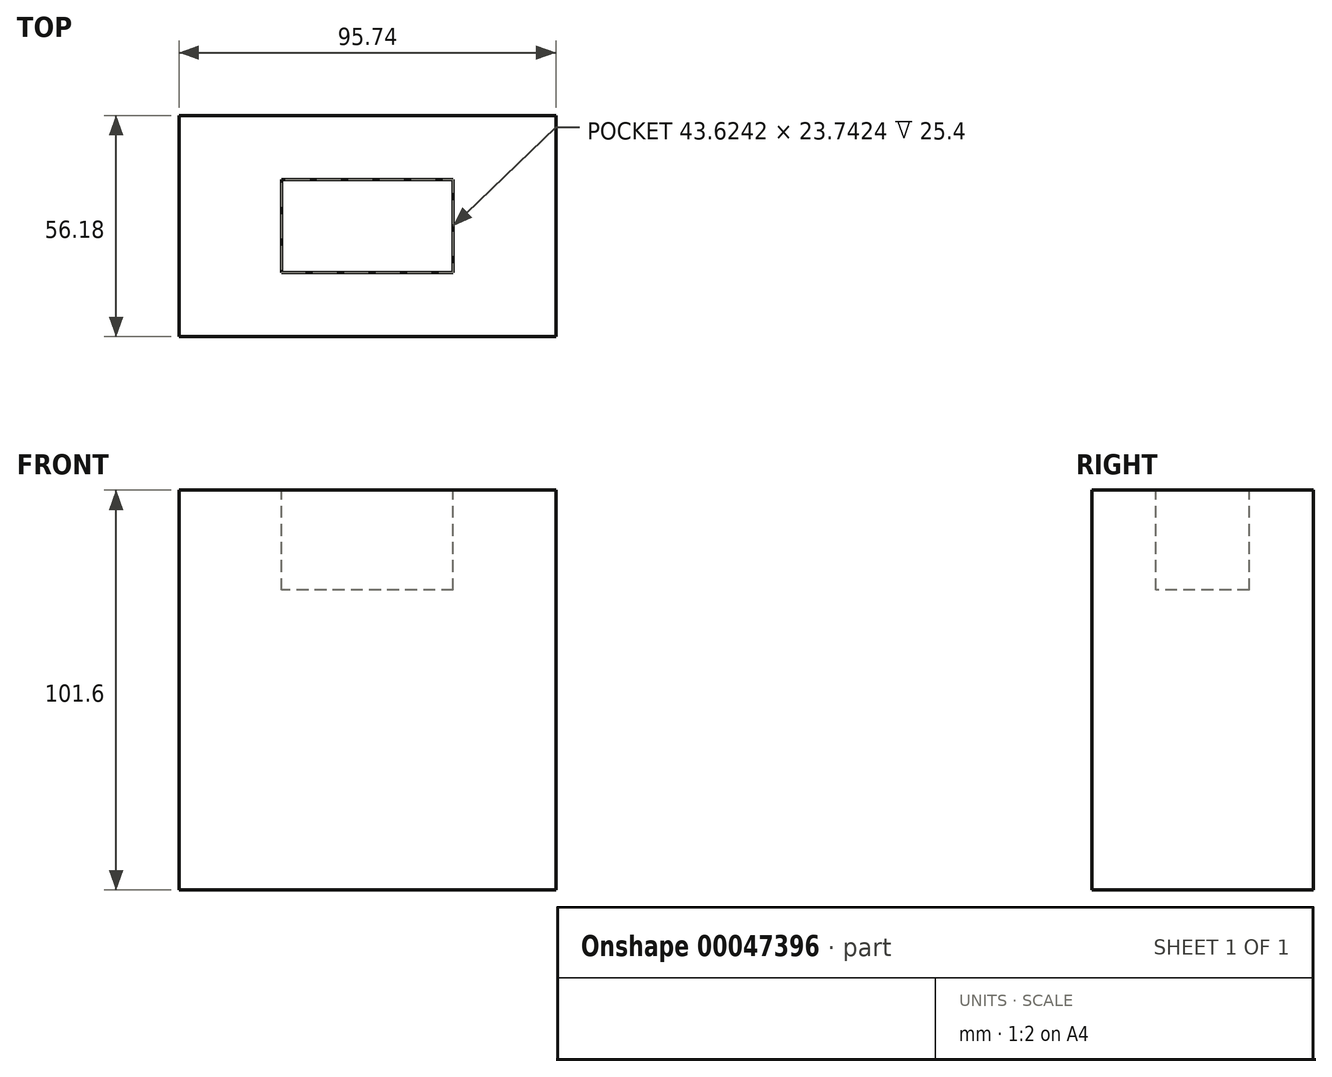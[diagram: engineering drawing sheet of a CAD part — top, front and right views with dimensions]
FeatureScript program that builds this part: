
annotation { "Feature Type Name" : "Feature", "Feature Type Description" : "" }
export const myFeature = defineFeature(function(context is Context, id is Id, definition is map)
    precondition{}
    {
        {
            var Q0;
            Q0=qCreatedBy(makeId("Top.planeOp"),FACE);
            var sketch = newSketch(context, id + "F0", { "sketchPlane" : qUnion([Q0])});
            skLineSegment(sketch, "E0.rect.bottom", {"start": v(47.87, 28.09) * mm, "end": v(-47.87, 28.09) * mm});
            skLineSegment(sketch, "E0.rect.top", {"start": v(47.87, -28.09) * mm, "end": v(-47.87, -28.09) * mm});
            skLineSegment(sketch, "E0.rect.left", {"start": v(47.87, 28.09) * mm, "end": v(47.87, -28.09) * mm});
            skLineSegment(sketch, "E0.rect.right", {"start": v(-47.87, 28.09) * mm, "end": v(-47.87, -28.09) * mm});
            skPoint(sketch, "E0.rect.middle", {"position": v(0, 0) * mm});
            skSolve(sketch);
        }
        {
            var Q0;
            Q0=makeQuery(id+"F0.imprint","IMPRINT",FACE,{"disambiguationData":[TD([[makeQuery(id+"F0.imprint","IMPRINT",EDGE,{"derivedFrom":sQuery(id+"F0.wireOp",EDGE,"E0.rect.bottom")}),1.0]])]});
            var Q1;
            Q1 = qSketchRegion(id + "F0", true);
            extrude(context, id + "F1", {"entities" : qUnion([Q0, Q1]), "depth" : 76.2 * mm});
        }
        {
            var Q0;
            Q0=makeQuery(id+"F1.opExtrude","CAP_FACE",FACE,{"disambiguationData":[OSD([sQuery(id+"F0.wireOp",EDGE,"E0.rect.bottom"),sQuery(id+"F0.wireOp",EDGE,"E0.rect.top"),sQuery(id+"F0.wireOp",EDGE,"E0.rect.left"),sQuery(id+"F0.wireOp",EDGE,"E0.rect.right")])],"isStart":false});
            extrude(context, id + "F2", {"entities" : qUnion([Q0]), "operationType" : NewBodyOperationType.ADD, "depth" : 25.4 * mm});
        }
        {
            var Q0;
            Q0=makeQuery(id+"F2.opExtrude","CAP_FACE",FACE,{"disambiguationData":[OSD([sQuery(id+"F0.wireOp",EDGE,"E0.rect.bottom"),sQuery(id+"F0.wireOp",EDGE,"E0.rect.top"),sQuery(id+"F0.wireOp",EDGE,"E0.rect.left"),sQuery(id+"F0.wireOp",EDGE,"E0.rect.right")])],"isStart":false});
            var sketch = newSketch(context, id + "F3", { "sketchPlane" : qUnion([Q0])});
            skLineSegment(sketch, "E1.rect.bottom", {"start": v(21.81, 11.87) * mm, "end": v(-21.81, 11.87) * mm});
            skLineSegment(sketch, "E1.rect.top", {"start": v(21.81, -11.87) * mm, "end": v(-21.81, -11.87) * mm});
            skLineSegment(sketch, "E1.rect.left", {"start": v(21.81, 11.87) * mm, "end": v(21.81, -11.87) * mm});
            skPoint(sketch, "E1.rect.middle", {"position": v(0, 0) * mm});
            skLineSegment(sketch, "E2", {"start": v(-21.81, 11.87) * mm, "end": v(-21.81, -11.87) * mm});
            skSolve(sketch);
        }
        {
            var Q0;
            Q0 = qSketchRegion(id + "F3", true);
            extrude(context, id + "F4", {"entities" : qUnion([Q0]), "operationType" : NewBodyOperationType.REMOVE, "oppositeDirection" : true, "depth" : 25.4 * mm});
        }
    });
